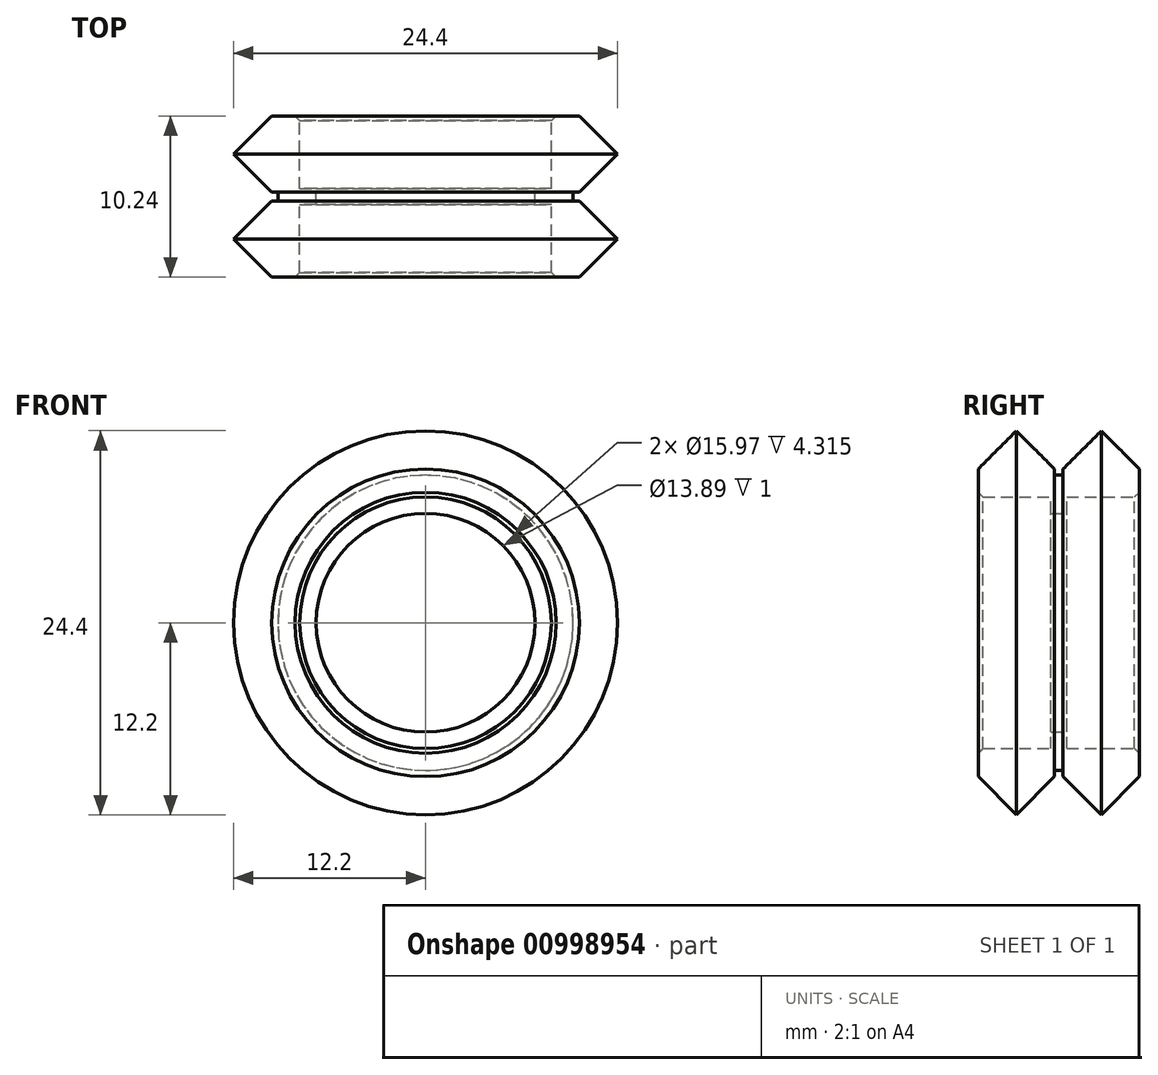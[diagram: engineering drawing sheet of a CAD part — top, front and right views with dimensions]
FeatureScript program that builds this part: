
annotation { "Feature Type Name" : "Feature", "Feature Type Description" : "" }
export const myFeature = defineFeature(function(context is Context, id is Id, definition is map)
    precondition{}
    {
        {
            var Q0;
            Q0=qCreatedBy(makeId("Front.planeOp"),FACE);
            var sketch = newSketch(context, id + "F0", { "sketchPlane" : qUnion([Q0])});
            skCircle(sketch, "E0", {"center": v(0, 0) * mm, "radius": 9.38 * mm});
            skCircle(sketch, "E1", {"center": v(0, 0) * mm, "radius": 7.99 * mm});
            skCircle(sketch, "E2", {"center": v(0, 0) * mm, "radius": 6.95 * mm});
            skSolve(sketch);
        }
        {
            var Q0;
            Q0=makeQuery(id+"F0.imprint","IMPRINT",FACE,{"disambiguationData":[TD([[makeQuery(id+"F0.imprint","IMPRINT",EDGE,{"derivedFrom":sQuery(id+"F0.wireOp",EDGE,"E0")}),1.0]])]});
            extrude(context, id + "F1", {"entities" : qUnion([Q0]), "endBound" : BoundingType.SYMMETRIC, "depth" : 10.23 * mm, "offsetDistance" : 25 * mm});
        }
        {
            var Q0;
            Q0=makeQuery(id+"F0.imprint","IMPRINT",FACE,{"disambiguationData":[TD([[makeQuery(id+"F0.imprint","IMPRINT",EDGE,{"derivedFrom":sQuery(id+"F0.wireOp",EDGE,"E1")}),1.0]])]});
            extrude(context, id + "F2", {"entities" : qUnion([Q0]), "operationType" : NewBodyOperationType.ADD, "endBound" : BoundingType.SYMMETRIC, "depth" : 1 * mm, "offsetDistance" : 25 * mm});
        }
        {
            var Q0;
            Q0=qCreatedBy(makeId("Right.planeOp"),FACE);
            var sketch = newSketch(context, id + "F3", { "sketchPlane" : qUnion([Q0])});
            skLineSegment(sketch, "E3", {"start": v(0, 0) * mm, "end": v(0, 9.38) * mm, "construction": true});
            skLineSegment(sketch, "E4", {"start": v(0, 9.38) * mm, "end": v(0.28, 9.38) * mm});
            skLineSegment(sketch, "E5", {"start": v(2.7, 12.2) * mm, "end": v(0.28, 9.77) * mm});
            skLineSegment(sketch, "E6", {"start": v(0.27, 9.77) * mm, "end": v(0.28, 9.38) * mm});
            skLineSegment(sketch, "E7", {"start": v(0.28, 9.38) * mm, "end": v(0, 9.38) * mm});
            skLineSegment(sketch, "E8", {"start": v(5.12, 9.38) * mm, "end": v(5.12, 9.77) * mm});
            skLineSegment(sketch, "E9", {"start": v(5.12, 9.77) * mm, "end": v(2.7, 12.2) * mm});
            skLineSegment(sketch, "E10", {"start": v(0.28, 9.38) * mm, "end": v(5.12, 9.38) * mm});
            skLineSegment(sketch, "E11.MirrorCS", {"start": v(0, 9.38) * mm, "end": v(-0.28, 9.38) * mm});
            skLineSegment(sketch, "E12.MirrorCS", {"start": v(-0.27, 9.77) * mm, "end": v(-0.28, 9.38) * mm});
            skLineSegment(sketch, "E13.MirrorCS", {"start": v(-2.7, 12.2) * mm, "end": v(-0.28, 9.77) * mm});
            skLineSegment(sketch, "E14.MirrorCS", {"start": v(-5.11, 9.77) * mm, "end": v(-2.7, 12.2) * mm});
            skLineSegment(sketch, "E15.MirrorCS", {"start": v(-5.12, 9.38) * mm, "end": v(-5.12, 9.77) * mm});
            skLineSegment(sketch, "E16.MirrorCS", {"start": v(-0.28, 9.38) * mm, "end": v(-5.12, 9.38) * mm});
            skSolve(sketch);
        }
        {
            var Q0;
            Q0=makeQuery(id+"F3.imprint","IMPRINT",FACE,{"disambiguationData":[TD([[makeQuery(id+"F3.imprint","IMPRINT",EDGE,{"derivedFrom":sQuery(id+"F3.wireOp",EDGE,"E5")}),1.0]])]});
            var Q1;
            Q1=makeQuery(id+"F3.imprint","IMPRINT",FACE,{"disambiguationData":[TD([[makeQuery(id+"F3.imprint","IMPRINT",EDGE,{"derivedFrom":sQuery(id+"F3.wireOp",EDGE,"E12.MirrorCS")}),-1.0]])]});
            var Q2;
            Q2=makeQuery(id+"F2.opExtrude","CAP_EDGE",EDGE,{"disambiguationData":[OSD([sQuery(id+"F0.wireOp",EDGE,"E2")])],"isStart":false});
            revolve(context, id + "F4", {"operationType" : NewBodyOperationType.ADD, "surfaceOperationType" : NewSurfaceOperationType.NEW, "entities" : qUnion([Q0, Q1]), "axis" : qUnion([Q2]), "revolveType" : RevolveType.FULL});
        }
        {
            var Q0;
            Q0=makeQuery(id+"F1.opExtrude","CAP_EDGE",EDGE,{"disambiguationData":[OSD([sQuery(id+"F0.wireOp",EDGE,"E1")])],"isStart":true});
            var Q1;
            Q1=makeQuery(id+"F1.opExtrude","CAP_EDGE",EDGE,{"disambiguationData":[OSD([sQuery(id+"F0.wireOp",EDGE,"E1")])],"isStart":false});
            chamfer(context, id + "F5", {"entities" : qUnion([Q0, Q1]), "width" : .3 * mm, "tangentPropagation" : true});
        }
    });
